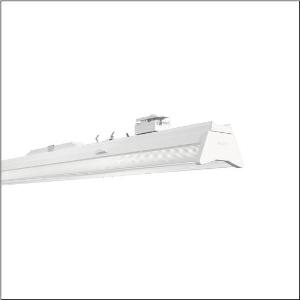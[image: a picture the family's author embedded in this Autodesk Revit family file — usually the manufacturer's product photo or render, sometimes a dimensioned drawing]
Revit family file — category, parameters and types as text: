
# Revit family: licross_r__21_performance_mo_52td167n445g_3390
name_source: partatom
category: Lighting Fixtures
units: mm (PartAtom-declared; Revit-internal decimal feet)

## family parameters
Cut with Voids When Loaded = No
Host = Face
Light Source = No
Part Type = Normal
Room Calculation Point = No
Round Connector Dimension = Use Diameter
Shared = No

## types (1)
- Licross® 21 Performance MO (1 x LED, 4580 lm, 24.7 W, 4000K)
    Apparent Load = 25 VA
    CIE Flux Codes = 66 88 96 79 100
    Color Rendering = 80
    Color Temperature = 4000K
    Default Elevation = 1800 mm
    Description = Licross® 21 Performance MO, luminaire insert, of sheet steel, galvanised, coil coated, white, length: 1.500mm, width: 120mm, height: 123mm, LED rated luminous flux: 4.580lm, light colour: 840, control gear: ON/OFF, with plug, 3-pole, with phase selection, mains connection: 220..240V, AC, 50/60Hz, rated input power: 25W, halogen-free wiring, primary light control with lens, of plastic, primary optical cover: cover, of PMMA, CAT 2 (L<= 3000cd/m²), light emission: direct/indirect distribution, primary light characteristic: symmetric, protection rating (complete): IP54, insulation class (complete): insulation class I (protective earthing), certification: CE, ENEC, UKCA, protection symbol: D if used in an environment with non-conductive dust loads with corresponding accessories, impact resistance: IK06, permissible ambient temperature for indoor applications: -35..+55°C, corresponds to IFS (International Featured Standards) requirements for safety and quality in the food industry, reducing of maximum allowable ambient temperature of 5°C with ceiling mounting, LABS conformity tested according to VDMA 24364:2018-05, packaging unit: 1 piece
    Height = 114 mm
    Lamp = 1 x LED
    Lamp Light Flux = 4580 lm
    Lamp Power = 24.7 W
    Lamp count = 1
    Length = 1500 mm
    Luminous efficacy = 185 lm/W
    Manufacturer = Siteco
    ModVariant = No
    Model = 52TD167N445G
    Mounting Place = Ceiling
    Mounting Type = Pendant
    Number of Poles = 1
    OnlyDefault = Yes
    Power Factor = 1
    Product Name = Licross® 21 Performance MO
    Product group = luminaire insert
    ProductGroupID = 901
    Protection Class = Protection class I
    Protection Degree = IP 54
    RLX_Detail_Level = 1
    RLX_Emergency_Light_Flux = 0 lm
    RLX_Emergency_Type = 0
    RLX_Emergency_Type_DB = No
    RlxData = <blob elided: 30465 chars, md5=9d3308a3>
    Socket = socket
    Standby Power = 0 W
    System Light Flux = 4580 lm
    System Power = 25 W
    Type Comments = Product without accessories
    Type Image = l_1256138.jpg
    URL = http://relux.com
    VarID = ---
    Voltage = 0 V
    Weight = 0.00 kg
    Width = 120 mm

## geometry (parser evidence)
native form markers: Blend x4, Sweep x14
no freeform markers — native parametric forms only
